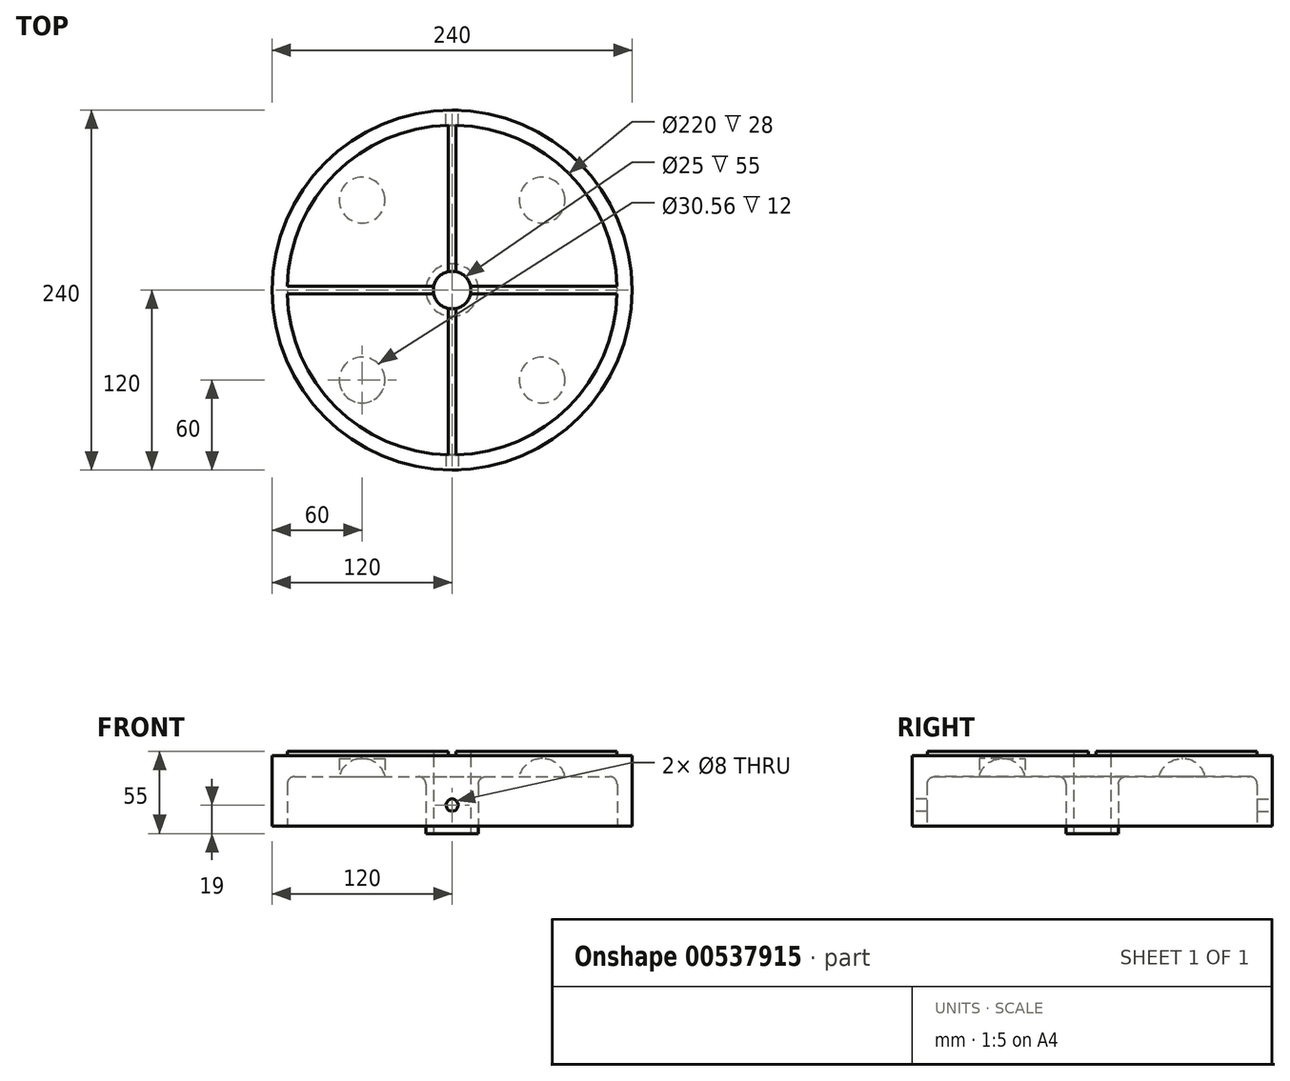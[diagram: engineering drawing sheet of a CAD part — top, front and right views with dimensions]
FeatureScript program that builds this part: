
annotation { "Feature Type Name" : "Feature", "Feature Type Description" : "" }
export const myFeature = defineFeature(function(context is Context, id is Id, definition is map)
    precondition{}
    {
        {
            var Q0;
            Q0=qCreatedBy(makeId("Top.planeOp"),FACE);
            var sketch = newSketch(context, id + "F0", { "sketchPlane" : qUnion([Q0])});
            skCircle(sketch, "E0", {"center": v(0, 0) * mm, "radius": 120 * mm});
            skSolve(sketch);
        }
        {
            var Q0;
            Q0 = qSketchRegion(id + "F0", true);
            extrude(context, id + "F1", {"entities" : qUnion([Q0]), "depth" : 12 * mm, "offsetDistance" : 25 * mm, "hasSecondDirection" : true, "secondDirectionOppositeDirection" : true, "secondDirectionDepth" : 38 * mm});
        }
        {
            var Q0;
            Q0=makeQuery(id+"F1.opExtrude","CAP_FACE",FACE,{"disambiguationData":[OSD([sQuery(id+"F0.wireOp",EDGE,"E0")])],"isStart":true});
            var sketch = newSketch(context, id + "F2", { "sketchPlane" : qUnion([Q0])});
            skCircle(sketch, "E1", {"center": v(0, 0) * mm, "radius": 110 * mm});
            skCircle(sketch, "E2", {"center": v(0, 0) * mm, "radius": 17.5 * mm});
            skSolve(sketch);
        }
        {
            var Q0;
            Q0 = qSketchRegion(id + "F2", true);
            extrude(context, id + "F3", {"entities" : qUnion([Q0]), "operationType" : NewBodyOperationType.REMOVE, "oppositeDirection" : true, "depth" : 38 * mm, "offsetDistance" : 25 * mm});
        }
        {
            var Q0;
            Q0=makeQuery(id+"F3.boolean.opBoolean","COPY",EDGE,{"derivedFrom":makeQuery(id+"F3.opExtrude","CAP_EDGE",EDGE,{"disambiguationData":[OSD([sQuery(id+"F2.wireOp",EDGE,"E2")])],"isStart":false})});
            var Q1;
            Q1=makeQuery(id+"F3.boolean.opBoolean","COPY",EDGE,{"derivedFrom":makeQuery(id+"F3.opExtrude","CAP_EDGE",EDGE,{"disambiguationData":[OSD([sQuery(id+"F2.wireOp",EDGE,"E1")])],"isStart":false})});
            fillet(context, id + "F4", {"entities" : qUnion([Q0, Q1]), "radius" : 5 * mm, "tangentPropagation" : true, "allowEdgeOverflow" : false});
        }
        {
            var Q0;
            Q0=makeQuery(id+"F3.boolean.opBoolean","COPY",FACE,{"derivedFrom":makeQuery(id+"F3.opExtrude","CAP_FACE",FACE,{"disambiguationData":[OSD([sQuery(id+"F2.wireOp",EDGE,"E1"),sQuery(id+"F2.wireOp",EDGE,"E2")])],"isStart":false})});
            var sketch = newSketch(context, id + "F5", { "sketchPlane" : qUnion([Q0])});
            skCircle(sketch, "E3", {"center": v(-60, 60) * mm, "radius": 15.28 * mm});
            skCircle(sketch, "E4.1.0", {"center": v(-60, -60) * mm, "radius": 15.28 * mm});
            skCircle(sketch, "E4.2.0", {"center": v(60, -60) * mm, "radius": 15.28 * mm});
            skCircle(sketch, "E4.3.0", {"center": v(60, 60) * mm, "radius": 15.28 * mm});
            skPoint(sketch, "E4.center", {"position": v(0, 0) * mm});
            skSolve(sketch);
        }
        {
            var Q0;
            Q0 = qSketchRegion(id + "F5", true);
            extrude(context, id + "F6", {"entities" : qUnion([Q0]), "operationType" : NewBodyOperationType.REMOVE, "oppositeDirection" : true, "depth" : 30.56 * mm / 2, "offsetDistance" : 25 * mm});
        }
        {
            var Q0;
            Q0=qCreatedBy(makeId("Front.planeOp"),FACE);
            cPlane(context, id + "F7", {"entities" : qUnion([Q0]), "cplaneType" : CPlaneType.OFFSET, "offset" : 120 * mm, "width" : 150 * mm, "height" : 150 * mm});
        }
        {
            var Q0;
            Q0=makeQuery(id+"F1.opExtrude","CAP_FACE",FACE,{"disambiguationData":[OSD([sQuery(id+"F0.wireOp",EDGE,"E0")])],"isStart":false});
            var sketch = newSketch(context, id + "F8", { "sketchPlane" : qUnion([Q0])});
            skCircle(sketch, "E5", {"center": v(0, 0) * mm, "radius": 120 * mm});
            skSolve(sketch);
        }
        {
            var Q0;
            Q0 = qSketchRegion(id + "F8", true);
            extrude(context, id + "F9", {"entities" : qUnion([Q0]), "operationType" : NewBodyOperationType.ADD, "depth" : 5 * mm, "offsetDistance" : 25 * mm});
        }
        {
            var Q0;
            Q0=makeQuery(id+"F3.boolean.opBoolean","SPLIT",FACE,{"disambiguationData":[TD([makeQuery(id+"F3.opExtrude","SWEPT_FACE",FACE,{"disambiguationData":[OSD([sQuery(id+"F2.wireOp",EDGE,"E2")])]})])],"derivedFrom":makeQuery(id+"F1.opExtrude","CAP_FACE",FACE,{"disambiguationData":[OSD([sQuery(id+"F0.wireOp",EDGE,"E0")])],"isStart":true})});
            var sketch = newSketch(context, id + "F10", { "sketchPlane" : qUnion([Q0])});
            skCircle(sketch, "E6", {"center": v(0, 0) * mm, "radius": 12.5 * mm});
            skSolve(sketch);
        }
        {
            var Q0;
            Q0 = qSketchRegion(id + "F10", true);
            extrude(context, id + "F11", {"entities" : qUnion([Q0]), "operationType" : NewBodyOperationType.REMOVE, "endBound" : BoundingType.THROUGH_ALL, "oppositeDirection" : true, "depth" : 25 * mm, "offsetDistance" : 25 * mm});
        }
        {
            var Q0;
            Q0=makeQuery(id+"F9.opExtrude","CAP_FACE",FACE,{"disambiguationData":[OSD([sQuery(id+"F8.wireOp",EDGE,"E5")])],"isStart":false});
            var sketch = newSketch(context, id + "F12", { "sketchPlane" : qUnion([Q0])});
            skCircle(sketch, "E7", {"center": v(0, 0) * mm, "radius": 120 * mm});
            skCircle(sketch, "E8", {"center": v(0, 0) * mm, "radius": 110 * mm});
            skSolve(sketch);
        }
        {
            var Q0;
            Q0 = qSketchRegion(id + "F12", true);
            extrude(context, id + "F13", {"entities" : qUnion([Q0]), "operationType" : NewBodyOperationType.REMOVE, "oppositeDirection" : true, "depth" : 3 * mm, "offsetDistance" : 25 * mm});
        }
        {
            var Q0;
            Q0=makeQuery(id+"F9.opExtrude","CAP_FACE",FACE,{"disambiguationData":[OSD([sQuery(id+"F8.wireOp",EDGE,"E5")])],"isStart":false});
            var sketch = newSketch(context, id + "F14", { "sketchPlane" : qUnion([Q0])});
            skLineSegment(sketch, "E9.bottom", {"start": v(-2.5, -125) * mm, "end": v(2.5, -125) * mm});
            skLineSegment(sketch, "E9.top", {"start": v(-2.5, 125) * mm, "end": v(2.5, 125) * mm});
            skLineSegment(sketch, "E9.left", {"start": v(-2.5, -125) * mm, "end": v(-2.5, 125) * mm});
            skLineSegment(sketch, "E9.right", {"start": v(2.5, -125) * mm, "end": v(2.5, 125) * mm});
            skPoint(sketch, "E9.middle", {"position": v(0, 0) * mm});
            skLineSegment(sketch, "E10.1.0", {"start": v(-125, -2.5) * mm, "end": v(125, -2.5) * mm});
            skLineSegment(sketch, "E10.1.1", {"start": v(-125, 2.5) * mm, "end": v(125, 2.5) * mm});
            skLineSegment(sketch, "E10.1.2", {"start": v(125, 2.5) * mm, "end": v(125, -2.5) * mm});
            skLineSegment(sketch, "E10.1.3", {"start": v(-125, 2.5) * mm, "end": v(-125, -2.5) * mm});
            skLineSegment(sketch, "E10.anchor1", {"start": v(0, 0) * mm, "end": v(2.5, -125) * mm, "construction": true});
            skLineSegment(sketch, "E10.anchor2", {"start": v(0, 0) * mm, "end": v(-125, -2.5) * mm, "construction": true});
            skSolve(sketch);
        }
        {
            var Q0;
            Q0 = qSketchRegion(id + "F14", true);
            extrude(context, id + "F15", {"entities" : qUnion([Q0]), "operationType" : NewBodyOperationType.REMOVE, "oppositeDirection" : true, "depth" : 3 * mm, "offsetDistance" : 25 * mm});
        }
        {
            var Q0;
            Q0=makeQuery(id+"F1.opExtrude","CAP_FACE",FACE,{"disambiguationData":[OSD([sQuery(id+"F0.wireOp",EDGE,"E0")])],"isStart":true});
            var sketch = newSketch(context, id + "F16", { "sketchPlane" : qUnion([Q0])});
            skCircle(sketch, "E11", {"center": v(0, 0) * mm, "radius": 136.79 * mm});
            skCircle(sketch, "E12", {"center": v(0, 0) * mm, "radius": 100.94 * mm});
            skSolve(sketch);
        }
        {
            var Q0;
            Q0 = qSketchRegion(id + "F16", true);
            extrude(context, id + "F17", {"entities" : qUnion([Q0]), "operationType" : NewBodyOperationType.REMOVE, "oppositeDirection" : true, "depth" : 5 * mm, "offsetDistance" : 25 * mm});
        }
        {
            var Q0;
            Q0=makeQuery(id+"F6.boolean.opBoolean","INTERSECT",EDGE,{"derivedFrom":[makeQuery(id+"F1.opExtrude","CAP_FACE",FACE,{"disambiguationData":[OSD([sQuery(id+"F0.wireOp",EDGE,"E0")])],"isStart":false}),makeQuery(id+"F6.opExtrude","SWEPT_FACE",FACE,{"disambiguationData":[OSD([sQuery(id+"F5.wireOp",EDGE,"E4.3.0")])]})]});
            var Q1;
            Q1=makeQuery(id+"F6.boolean.opBoolean","INTERSECT",EDGE,{"derivedFrom":[makeQuery(id+"F1.opExtrude","CAP_FACE",FACE,{"disambiguationData":[OSD([sQuery(id+"F0.wireOp",EDGE,"E0")])],"isStart":false}),makeQuery(id+"F6.opExtrude","SWEPT_FACE",FACE,{"disambiguationData":[OSD([sQuery(id+"F5.wireOp",EDGE,"E3")])]})]});
            var Q2;
            Q2=makeQuery(id+"F6.boolean.opBoolean","INTERSECT",EDGE,{"derivedFrom":[makeQuery(id+"F1.opExtrude","CAP_FACE",FACE,{"disambiguationData":[OSD([sQuery(id+"F0.wireOp",EDGE,"E0")])],"isStart":false}),makeQuery(id+"F6.opExtrude","SWEPT_FACE",FACE,{"disambiguationData":[OSD([sQuery(id+"F5.wireOp",EDGE,"E4.1.0")])]})]});
            var Q3;
            Q3=makeQuery(id+"F6.boolean.opBoolean","INTERSECT",EDGE,{"derivedFrom":[makeQuery(id+"F1.opExtrude","CAP_FACE",FACE,{"disambiguationData":[OSD([sQuery(id+"F0.wireOp",EDGE,"E0")])],"isStart":false}),makeQuery(id+"F6.opExtrude","SWEPT_FACE",FACE,{"disambiguationData":[OSD([sQuery(id+"F5.wireOp",EDGE,"E4.2.0")])]})]});
            fillet(context, id + "F18", {"entities" : qUnion([Q0, Q1, Q2, Q3]), "radius" : (30.56 / 2) * mm, "tangentPropagation" : true, "allowEdgeOverflow" : false});
        }
        {
            var Q0;
            Q0=qCreatedBy(id+"F7.planeOp",FACE);
            var sketch = newSketch(context, id + "F19", { "sketchPlane" : qUnion([Q0])});
            skCircle(sketch, "E13", {"center": v(0, -19) * mm, "radius": 4 * mm});
            skSolve(sketch);
        }
        {
            var Q0;
            Q0 = qSketchRegion(id + "F19", true);
            extrude(context, id + "F20", {"entities" : qUnion([Q0]), "operationType" : NewBodyOperationType.REMOVE, "oppositeDirection" : true, "depth" : 25 * mm, "offsetDistance" : 25 * mm});
        }
        {
            var Q0;
            Q0=qCreatedBy(makeId("Front.planeOp"),FACE);
            cPlane(context, id + "F21", {"entities" : qUnion([Q0]), "cplaneType" : CPlaneType.OFFSET, "offset" : 120 * mm, "oppositeDirection" : true, "width" : 150 * mm, "height" : 150 * mm});
        }
        {
            var Q0;
            Q0=qCreatedBy(id+"F21.planeOp",FACE);
            var sketch = newSketch(context, id + "F22", { "sketchPlane" : qUnion([Q0])});
            skCircle(sketch, "E14", {"center": v(0, -19) * mm, "radius": 4 * mm});
            skSolve(sketch);
        }
        {
            var Q0;
            Q0 = qSketchRegion(id + "F22", true);
            extrude(context, id + "F23", {"entities" : qUnion([Q0]), "operationType" : NewBodyOperationType.REMOVE, "depth" : 25 * mm, "offsetDistance" : 25 * mm});
        }
    });
